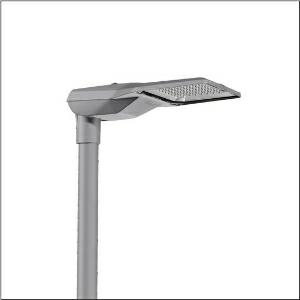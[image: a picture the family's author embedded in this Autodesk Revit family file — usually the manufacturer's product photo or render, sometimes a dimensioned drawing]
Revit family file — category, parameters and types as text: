
# Revit family: streetlight_sl_21_midi___st1_0a_5xe3d33s08lb_350a
name_source: partatom
category: Lighting Fixtures
units: mm (PartAtom-declared; Revit-internal decimal feet)

## family parameters
Cut with Voids When Loaded = No
Host = Face
Light Source = No
Part Type = Normal
Room Calculation Point = No
Round Connector Dimension = Use Diameter
Shared = No

## types (1)
- --- (1 x LED, 14340 lm, 99.6 W, 3000K)
    Apparent Load = 100 VA
    CIE Flux Codes = 37 72 97 100 100
    Color Rendering = 70
    Color Temperature = 3000K
    Default Elevation = 1800 mm
    Description = Streetlight SL 21 midi, mast luminaire, primary light control with lens, of PMMA, primary optical cover: cover, of toughened safety glass, transparent, light distribution: ST1.0a, light emission: direct distribution, primary light characteristic: asymmetric, installation type: side-entry, post-top, LED, High Power LED, rated luminous flux: 14.340lm, luminous efficacy: 144lm/W, light colour: 730, colour temperature: 3000K, control gear: D4i, control: flexible luminous flux parameterisation, time-dependent luminous flux control, constant luminous flux control, overheat protection, pre-setting: logarithmic dimming characteristic, mains connection: 230..240V, AC, 50/60Hz, start of lifetime: 100W, end of service life: 102W, reduction: 46W, luminaire housing, of diecast aluminium, powder-coated, SITECO metallic grey (DB 702S), corrosivity category C5 high according to DIN EN ISO 12944, please order mast flange separately, inclination adjustable: 0°, 5°, 10°, 15°, sealing non-destructively replaceable, multi-level sealing system, length: 644mm, width: 335mm, height: 110mm, mast flange for spigot size: 42mm (side-entry): 5XC10008XM4, 60/48mm (side-entry/post-top): 5XC10108XM2, 76/60mm (side-entry/post-top): 5XC10108XM1, mounting height: 4..8m, Smart Interface above, protection rating (complete): IP66, insulation class (complete): insulation class II (safety insulation), certification: CE, ENEC, ENEC+, VDE, impact resistance: IK10, permissible operating ambient temperature for outdoor applications: -40..+50°C, standard-compliant lighting for roads and squares, packaging unit: 1 piece

Light Distribution: ST1.0a
    Height = 111 mm
    Lamp = 1 x LED
    Lamp Light Flux = 14340 lm
    Lamp Power = 99.6 W
    Lamp count = 1
    Length = 644 mm
    Luminous efficacy = 144 lm/W
    Manufacturer = Siteco
    ModVariant = No
    Model = 5XE3D33S08LB
    Number of Poles = 1
    OnlyDefault = Yes
    Power Factor = 1
    Product Name = Streetlight SL 21 midi | ST1.0a
    Product group = mast luminaire | pylon top
    ProductGroupID = 6100
    Protection Class = Protection class II
    Protection Degree = IP 66
    RLX_Detail_Level = 1
    RLX_Emergency_Light_Flux = 0 lm
    RLX_Emergency_Type = 0
    RLX_Emergency_Type_DB = No
    RlxData = <blob elided: 26801 chars, md5=da66cfb6>
    Socket = socket
    Standby Power = 0 W
    System Light Flux = 14340 lm
    System Power = 100 W
    Type Comments = factory setting: luminous flux: 100 % | dim-lin: 254 | 1020 mA
    Type Image = l_1004302.jpg
    URL = http://relux.com
    VarID = @adj_031691
    Voltage = 0 V
    Weight = 0.00 kg
    Width = 336 mm

## geometry (parser evidence)
native form markers: Blend x4, Sweep x12
no freeform markers — native parametric forms only
